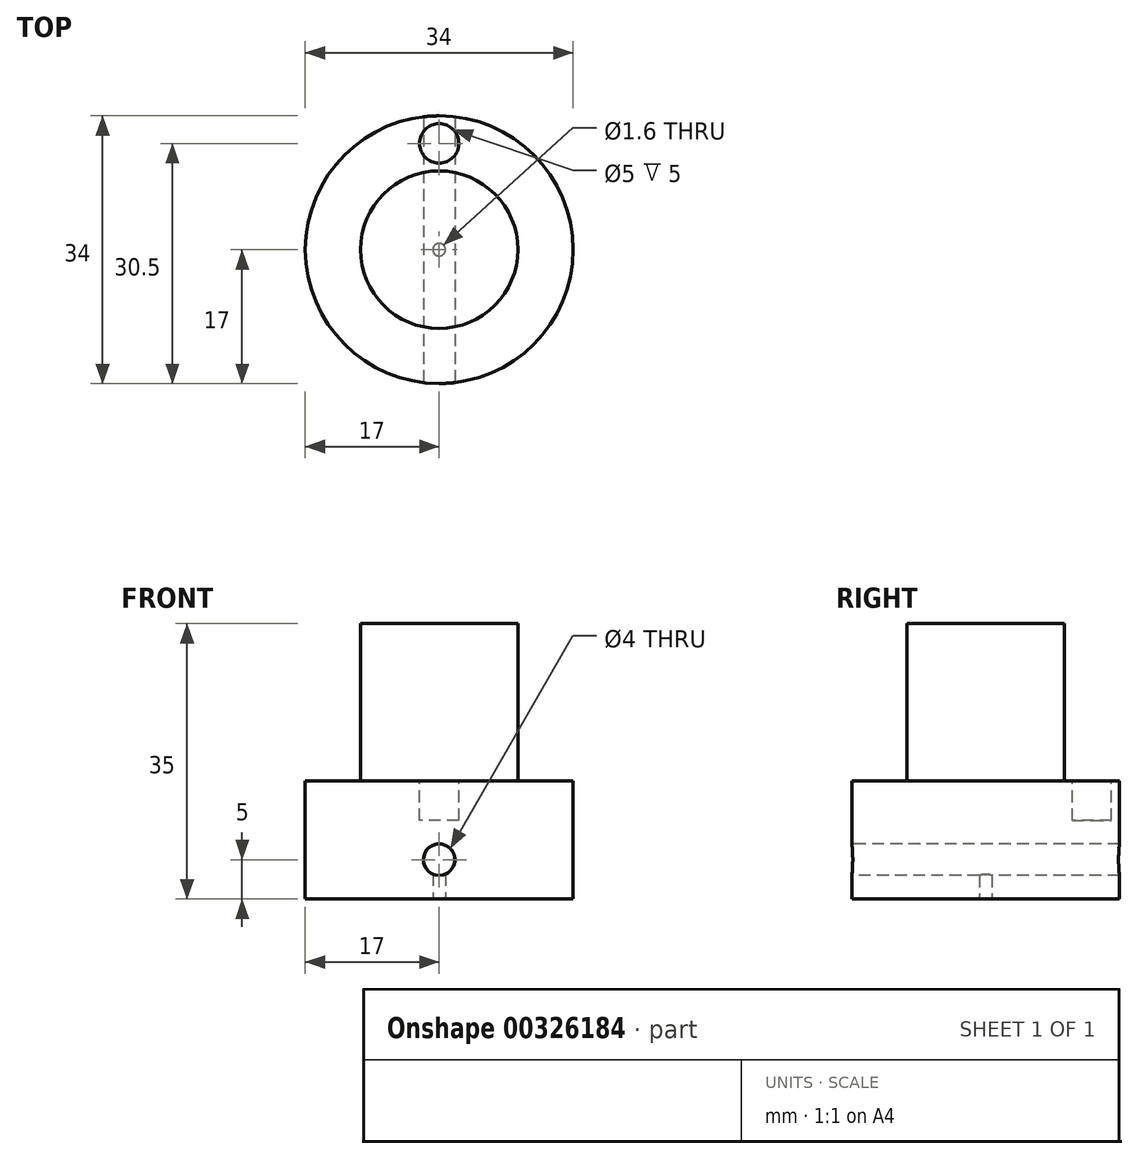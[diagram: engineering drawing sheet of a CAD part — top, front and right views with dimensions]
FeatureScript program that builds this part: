
annotation { "Feature Type Name" : "Feature", "Feature Type Description" : "" }
export const myFeature = defineFeature(function(context is Context, id is Id, definition is map)
    precondition{}
    {
        {
            var Q0;
            Q0=qCreatedBy(makeId("Top.planeOp"),FACE);
            var sketch = newSketch(context, id + "F0", { "sketchPlane" : qUnion([Q0])});
            skCircle(sketch, "E0", {"center": v(0, 0) * mm, "radius": 17 * mm});
            skSolve(sketch);
        }
        {
            var Q0;
            Q0=makeQuery(id+"F0.imprint","IMPRINT",FACE,{"disambiguationData":[TD([[makeQuery(id+"F0.imprint","IMPRINT",EDGE,{"derivedFrom":sQuery(id+"F0.wireOp",EDGE,"E0")}),1.0]])]});
            extrude(context, id + "F1", {"entities" : qUnion([Q0]), "depth" : 15 * mm});
        }
        {
            var Q0;
            Q0=makeQuery(id+"F1.opExtrude","CAP_FACE",FACE,{"disambiguationData":[OSD([sQuery(id+"F0.wireOp",EDGE,"E0")])],"isStart":false});
            var sketch = newSketch(context, id + "F2", { "sketchPlane" : qUnion([Q0])});
            skCircle(sketch, "E1", {"center": v(0, 0) * mm, "radius": 10 * mm});
            skSolve(sketch);
        }
        {
            var Q0;
            Q0=makeQuery(id+"F2.imprint","IMPRINT",FACE,{"disambiguationData":[TD([[makeQuery(id+"F2.imprint","IMPRINT",EDGE,{"derivedFrom":sQuery(id+"F2.wireOp",EDGE,"E1")}),1.0]])]});
            extrude(context, id + "F3", {"entities" : qUnion([Q0]), "operationType" : NewBodyOperationType.ADD, "depth" : 20 * mm});
        }
        {
            var Q0;
            Q0=makeQuery(id+"F1.opExtrude","CAP_FACE",FACE,{"disambiguationData":[OSD([sQuery(id+"F0.wireOp",EDGE,"E0")])],"isStart":true});
            var sketch = newSketch(context, id + "F4", { "sketchPlane" : qUnion([Q0])});
            skCircle(sketch, "E2", {"center": v(0, 0) * mm, "radius": 0.8 * mm});
            skSolve(sketch);
        }
        {
            var Q0;
            Q0=makeQuery(id+"F4.imprint","IMPRINT",FACE,{"disambiguationData":[TD([[makeQuery(id+"F4.imprint","IMPRINT",EDGE,{"derivedFrom":sQuery(id+"F4.wireOp",EDGE,"E2")}),1.0]])]});
            extrude(context, id + "F5", {"entities" : qUnion([Q0]), "operationType" : NewBodyOperationType.REMOVE, "oppositeDirection" : true, "depth" : 5 * mm});
        }
        {
            var Q0;
            Q0=qCreatedBy(makeId("Front.planeOp"),FACE);
            cPlane(context, id + "F6", {"entities" : qUnion([Q0]), "cplaneType" : CPlaneType.OFFSET, "offset" : 25 * mm, "width" : 150 * mm, "height" : 150 * mm});
        }
        {
            var Q0;
            Q0=qCreatedBy(id+"F6.planeOp",FACE);
            var sketch = newSketch(context, id + "F7", { "sketchPlane" : qUnion([Q0])});
            skCircle(sketch, "E3", {"center": v(0, 5) * mm, "radius": 2 * mm});
            skSolve(sketch);
        }
        {
            var Q0;
            Q0=makeQuery(id+"F7.imprint","IMPRINT",FACE,{"disambiguationData":[TD([[makeQuery(id+"F7.imprint","IMPRINT",EDGE,{"derivedFrom":sQuery(id+"F7.wireOp",EDGE,"E3")}),1.0]])]});
            extrude(context, id + "F8", {"entities" : qUnion([Q0]), "operationType" : NewBodyOperationType.REMOVE, "endBound" : BoundingType.THROUGH_ALL, "oppositeDirection" : true, "depth" : 25 * mm});
        }
        {
            var Q0;
            Q0=makeQuery(id+"F1.opExtrude","CAP_FACE",FACE,{"disambiguationData":[OSD([sQuery(id+"F0.wireOp",EDGE,"E0")])],"isStart":false});
            var sketch = newSketch(context, id + "F9", { "sketchPlane" : qUnion([Q0])});
            skCircle(sketch, "E4", {"center": v(0, 13.5) * mm, "radius": 2.5 * mm});
            skSolve(sketch);
        }
        {
            var Q0;
            Q0=makeQuery(id+"F9.imprint","IMPRINT",FACE,{"disambiguationData":[TD([[makeQuery(id+"F9.imprint","IMPRINT",EDGE,{"derivedFrom":sQuery(id+"F9.wireOp",EDGE,"E4")}),1.0]])]});
            extrude(context, id + "F10", {"entities" : qUnion([Q0]), "operationType" : NewBodyOperationType.REMOVE, "oppositeDirection" : true, "depth" : 5 * mm, "offsetDistance" : 25 * mm});
        }
    });
